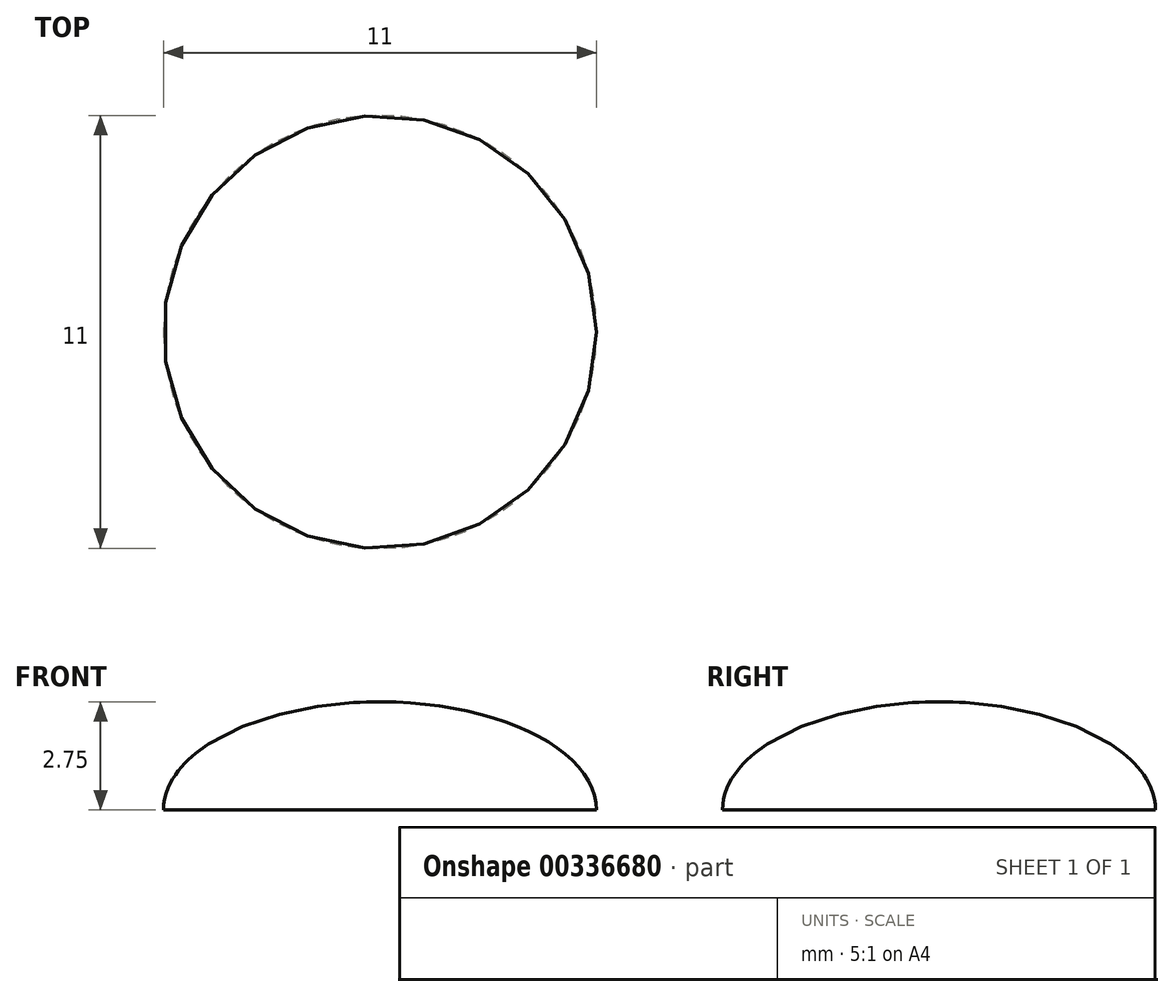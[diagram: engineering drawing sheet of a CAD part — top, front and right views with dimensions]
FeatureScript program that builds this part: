
annotation { "Feature Type Name" : "Feature", "Feature Type Description" : "" }
export const myFeature = defineFeature(function(context is Context, id is Id, definition is map)
    precondition{}
    {
        {
            var Q0;
            Q0=qCreatedBy(makeId("Front.planeOp"),FACE);
            var sketch = newSketch(context, id + "F0", { "sketchPlane" : qUnion([Q0])});
            skEllipse(sketch, "E0", {"center": v(0, 0) * mm, "majorRadius": 5.5 * mm, "minorRadius": 2.75 * mm, "majorAxis": v(1, 0)});
            skLineSegment(sketch, "E1.bottom", {"start": v(0, 0) * mm, "end": v(6.87, 0) * mm});
            skLineSegment(sketch, "E1.top", {"start": v(0, -3.78) * mm, "end": v(6.87, -3.78) * mm});
            skLineSegment(sketch, "E1.left", {"start": v(0, 0) * mm, "end": v(0, -3.78) * mm});
            skLineSegment(sketch, "E1.right", {"start": v(6.87, 0) * mm, "end": v(6.87, -3.78) * mm});
            skLineSegment(sketch, "E2.bottom", {"start": v(0, 0) * mm, "end": v(-8.93, 0) * mm});
            skLineSegment(sketch, "E2.top", {"start": v(0, -5.16) * mm, "end": v(-8.93, -5.16) * mm});
            skLineSegment(sketch, "E2.left", {"start": v(0, 0) * mm, "end": v(0, -5.16) * mm});
            skLineSegment(sketch, "E2.right", {"start": v(-8.93, 0) * mm, "end": v(-8.93, -5.16) * mm});
            skLineSegment(sketch, "E3.bottom", {"start": v(0, 0) * mm, "end": v(-9.65, 0) * mm});
            skLineSegment(sketch, "E3.top", {"start": v(0, 2.75) * mm, "end": v(-9.65, 2.75) * mm});
            skLineSegment(sketch, "E3.left", {"start": v(0, 0) * mm, "end": v(0, 2.75) * mm});
            skLineSegment(sketch, "E3.right", {"start": v(-9.65, 0) * mm, "end": v(-9.65, 2.75) * mm});
            skSolve(sketch);
        }
        {
            var Q0;
            {var subQ0=sQuery(id+"F0.wireOp",EDGE,"E3.left");Q0=makeQuery(id+"F0.imprint","IMPRINT",FACE,{"disambiguationData":[TD([[makeQuery(id+"F0.imprint","IMPRINT",EDGE,{"derivedFrom":subQ0}),-1.0]])]});}
            var Q1;
            Q1=sQuery(id+"F0.wireOp",EDGE,"E3.left");
            revolve(context, id + "F1", {"entities" : qUnion([Q0]), "axis" : qUnion([Q1]), "revolveType" : RevolveType.FULL});
        }
    });
